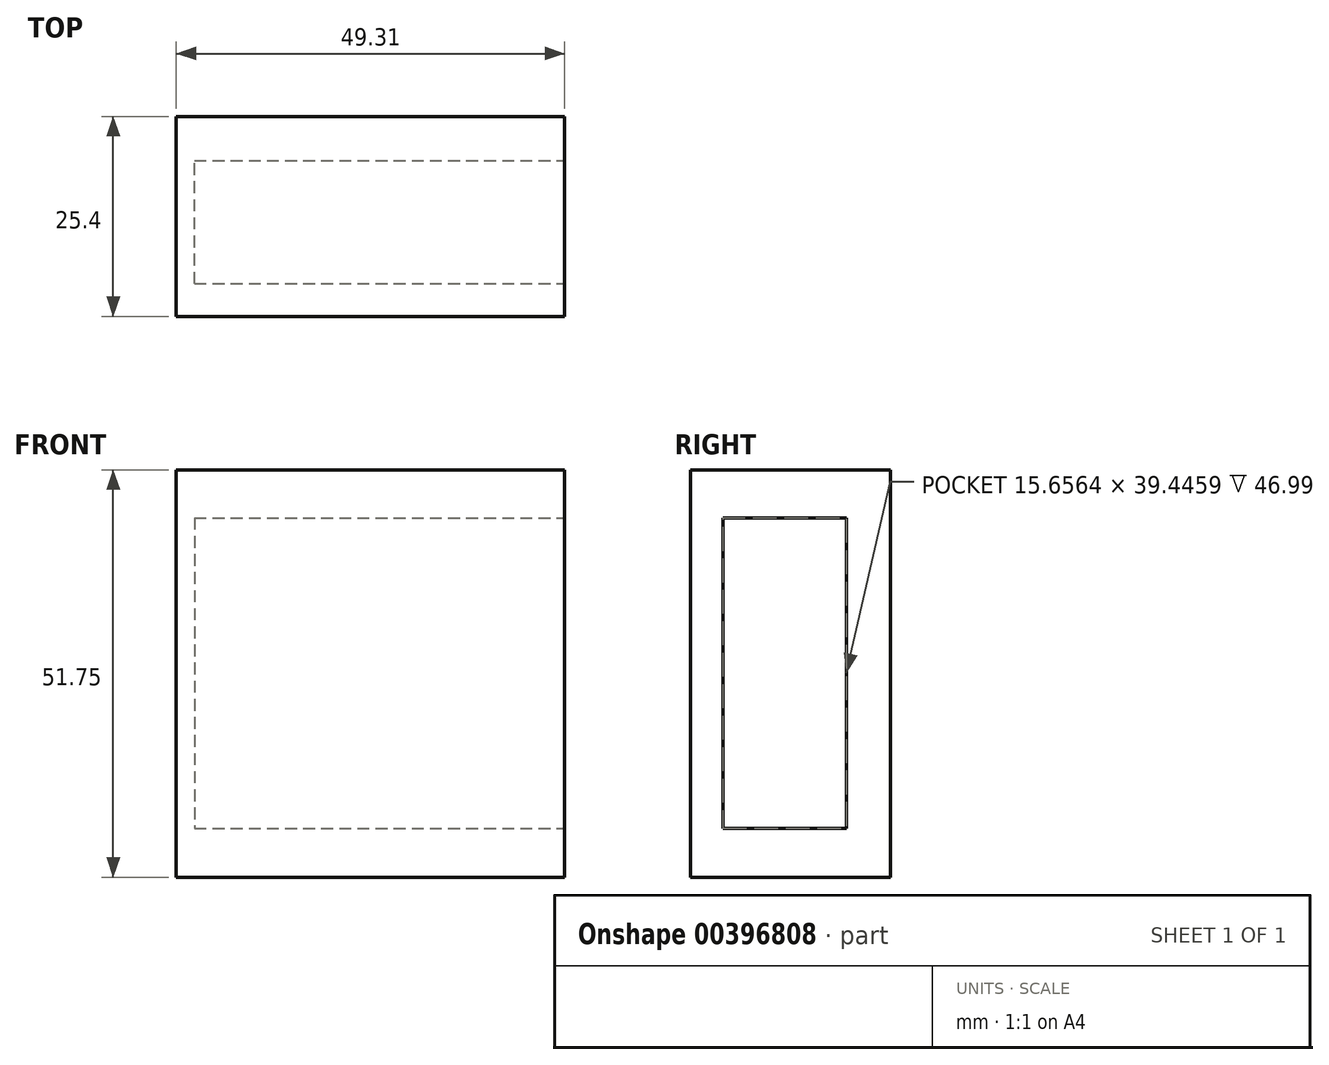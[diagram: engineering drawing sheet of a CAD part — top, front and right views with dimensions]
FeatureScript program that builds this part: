
annotation { "Feature Type Name" : "Feature", "Feature Type Description" : "" }
export const myFeature = defineFeature(function(context is Context, id is Id, definition is map)
    precondition{}
    {
        {
            var Q0;
            Q0=qCreatedBy(makeId("Front.planeOp"),FACE);
            var sketch = newSketch(context, id + "F0", { "sketchPlane" : qUnion([Q0])});
            skLineSegment(sketch, "E0.bottom", {"start": v(0, 0) * mm, "end": v(-49.3, 0) * mm});
            skLineSegment(sketch, "E0.top", {"start": v(0, 51.75) * mm, "end": v(-49.3, 51.75) * mm});
            skLineSegment(sketch, "E0.left", {"start": v(0, 0) * mm, "end": v(0, 51.75) * mm});
            skLineSegment(sketch, "E0.right", {"start": v(-49.3, 0) * mm, "end": v(-49.3, 51.75) * mm});
            skSolve(sketch);
        }
        {
            var Q0;
            Q0 = qSketchRegion(id + "F0", true);
            extrude(context, id + "F1", {"entities" : qUnion([Q0]), "depth" : 25.4 * mm});
        }
        {
            var Q0;
            Q0=makeQuery(id+"F1.opExtrude","SWEPT_FACE",FACE,{"disambiguationData":[OSD([sQuery(id+"F0.wireOp",EDGE,"E0.left")])]});
            var sketch = newSketch(context, id + "F2", { "sketchPlane" : qUnion([Q0])});
            skLineSegment(sketch, "E1.bottom", {"start": v(-21.25, 45.65) * mm, "end": v(-5.6, 45.65) * mm});
            skLineSegment(sketch, "E1.top", {"start": v(-21.25, 6.2) * mm, "end": v(-5.6, 6.2) * mm});
            skLineSegment(sketch, "E1.left", {"start": v(-21.25, 45.65) * mm, "end": v(-21.25, 6.2) * mm});
            skLineSegment(sketch, "E1.right", {"start": v(-5.6, 45.65) * mm, "end": v(-5.6, 6.2) * mm});
            skSolve(sketch);
        }
        {
            var Q0;
            Q0 = qSketchRegion(id + "F2", true);
            extrude(context, id + "F3", {"entities" : qUnion([Q0]), "operationType" : NewBodyOperationType.REMOVE, "oppositeDirection" : true, "depth" : 47 * mm});
        }
    });
